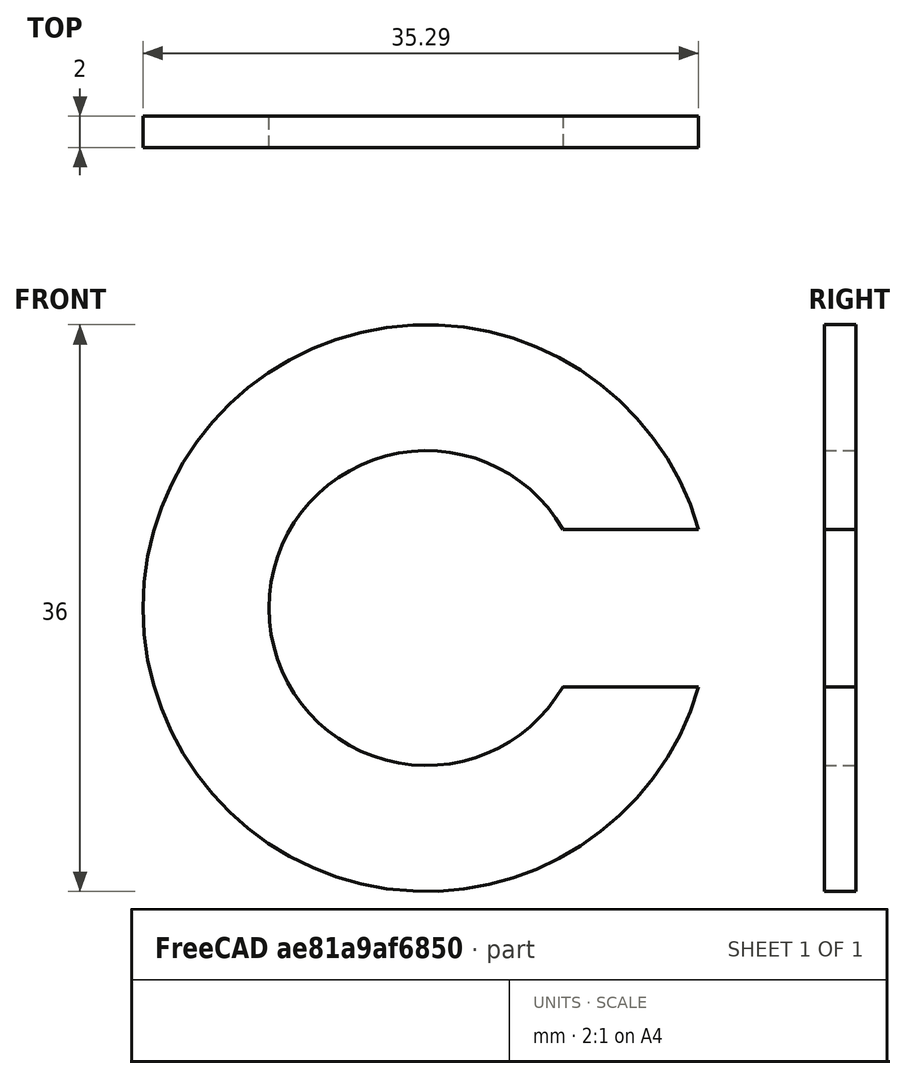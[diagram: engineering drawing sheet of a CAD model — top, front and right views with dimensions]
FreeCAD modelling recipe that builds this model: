
FCSTD DOCUMENT  (FreeCAD 0.20R29603 (Git))
Label: flam
License: All rights reserved
LicenseURL: http://en.wikipedia.org/wiki/All_rights_reserved
objects: Sketcher::SketchObject×1, PartDesign::Pad×1, PartDesign::Body×1
note: 4 computed .brp shape members not serialized (recipe doc carries the construction recipe); baked Part::Feature solids carry a one-line shape summary decoded from their .brp

FEATURE [Sketcher::SketchObject] Sketch
  FullyConstrained = true
  MapMode = 5
  Placement = pos=(0,0,0) rot=(1,0,0;1.5708rad)
  Support = -> [XZ_Plane]
  sketch-geometry (4):
    g0: ArcOfCircle CenterX=0 CenterY=0 CenterZ=0 NormalX=0 NormalY=0 NormalZ=1 AngleXU=0 Radius=18 StartAngle=0.28148 EndAngle=6.00171
    g1: LineSegment StartX=17.2916 StartY=5 StartZ=0 EndX=8.66025 EndY=5 EndZ=0
    g2: LineSegment StartX=8.66025 StartY=-5 StartZ=0 EndX=17.2916 EndY=-5 EndZ=0
    g3: ArcOfCircle CenterX=0 CenterY=0 CenterZ=0 NormalX=0 NormalY=0 NormalZ=1 AngleXU=0 Radius=10 StartAngle=0.523599 EndAngle=5.75959
  constraints (12):
    c: Coincident(g0,g-1)
    c: Diameter(g0) = 36
    c: Coincident(g1,g0)
    c: Horizontal(g1)
    c: Coincident(g2,g0)
    c: Horizontal(g2)
    c: DistanceY(g2,g1) = 10
    c: DistanceY(g0,g1) = 5
    c: Coincident(g3,g0)
    c: Coincident(g3,g1)
    c: Coincident(g3,g2)
    c: Diameter(g3) = 20
FEATURE [PartDesign::Pad] Pad
  Direction = (0,-1,2e-16)
  Length = 2
  Length2 = 10
  Placement = pos=(0,0,0) rot=(1,0,0;1.5708rad)
  Profile = -> Sketch
  ReferenceAxis = -> Sketch [N_Axis]
  Type = 0
FEATURE [PartDesign::Body] Body
  Group = -> [Sketch,Pad]
  Origin = -> Origin
  Tip = -> Pad
